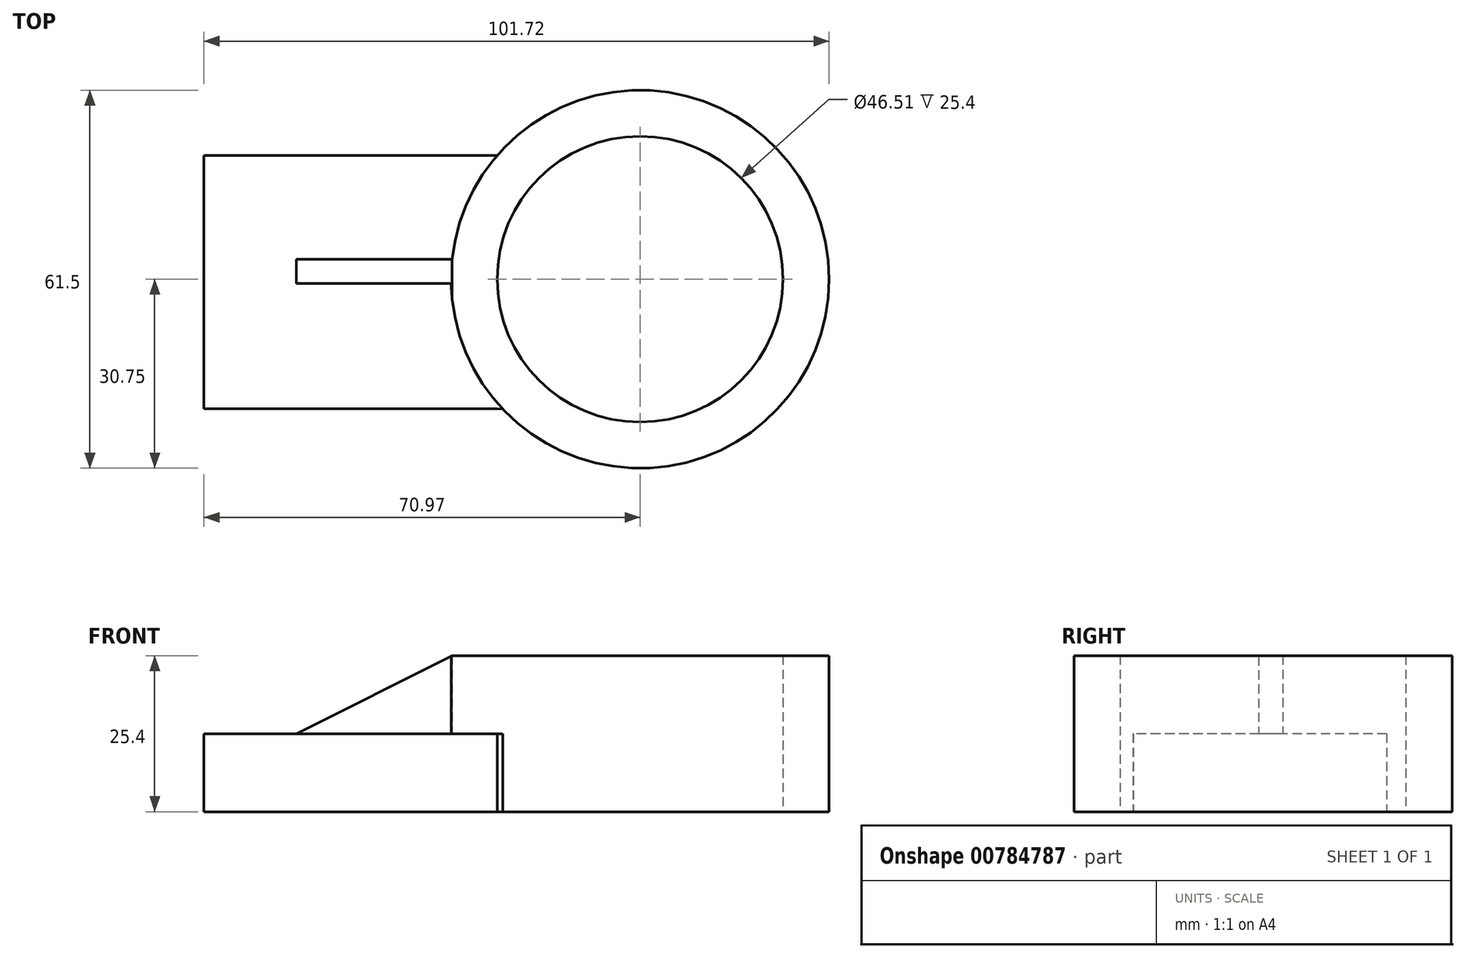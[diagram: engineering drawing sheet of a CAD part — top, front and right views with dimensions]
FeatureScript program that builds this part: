
annotation { "Feature Type Name" : "Feature", "Feature Type Description" : "" }
export const myFeature = defineFeature(function(context is Context, id is Id, definition is map)
    precondition{}
    {
        {
            var Q0;
            Q0=qCreatedBy(makeId("Top.planeOp"),FACE);
            var sketch = newSketch(context, id + "F0", { "sketchPlane" : qUnion([Q0])});
            skLineSegment(sketch, "E0.bottom", {"start": v(-70.97, 20.12) * mm, "end": v(-23.26, 20.12) * mm});
            skLineSegment(sketch, "E0.top", {"start": v(-70.97, -21.09) * mm, "end": v(-23.26, -21.09) * mm});
            skLineSegment(sketch, "E0.left", {"start": v(-70.97, 20.12) * mm, "end": v(-70.97, -21.09) * mm});
            skCircle(sketch, "E1", {"center": v(0, 0) * mm, "radius": 23.26 * mm});
            skCircle(sketch, "E2", {"center": v(0, 0) * mm, "radius": 30.75 * mm});
            skLineSegment(sketch, "E3", {"start": v(-23.26, -21.09) * mm, "end": v(-22.34, -21.13) * mm});
            skSolve(sketch);
        }
        {
            var Q0;
            Q0=makeQuery(id+"F0.imprint","IMPRINT",FACE,{"disambiguationData":[TD([[makeQuery(id+"F0.imprint","IMPRINT",EDGE,{"derivedFrom":sQuery(id+"F0.wireOp",EDGE,"E1")}),-1.0]])]});
            extrude(context, id + "F1", {"entities" : qUnion([Q0]), "depth" : 25.4 * mm, "offsetDistance" : 25.4 * mm});
        }
        {
            var Q0;
            {var subQ1=sQuery(id+"F0.wireOp",EDGE,"E0.bottom");Q0=makeQuery(id+"F0.imprint","IMPRINT",FACE,{"disambiguationData":[TD([[makeQuery(id+"F0.imprint","IMPRINT",EDGE,{"derivedFrom":subQ1}),-1.0]])]});}
            extrude(context, id + "F2", {"entities" : qUnion([Q0]), "operationType" : NewBodyOperationType.ADD, "depth" : 12.7 * mm, "offsetDistance" : 25.4 * mm});
        }
        {
            var Q0;
            Q0=makeQuery(id+"F2.opExtrude","CAP_FACE",FACE,{"disambiguationData":[OSD([sQuery(id+"F0.wireOp",EDGE,"E0.bottom"),sQuery(id+"F0.wireOp",EDGE,"E0.top"),sQuery(id+"F0.wireOp",EDGE,"E0.left"),sQuery(id+"F0.wireOp",EDGE,"E2"),sQuery(id+"F0.wireOp",EDGE,"E3")])],"isStart":false});
            var sketch = newSketch(context, id + "F3", { "sketchPlane" : qUnion([Q0])});
            skPoint(sketch, "E4.oppositeSnap0", {"position": v(-30.75, -0.68) * mm});
            skLineSegment(sketch, "E4.bottom", {"start": v(-30.58, 3.25) * mm, "end": v(-55.97, 3.25) * mm});
            skLineSegment(sketch, "E4.top", {"start": v(-30.58, -0.68) * mm, "end": v(-55.97, -0.68) * mm});
            skLineSegment(sketch, "E4.left", {"start": v(-30.58, 3.25) * mm, "end": v(-30.58, -0.68) * mm});
            skLineSegment(sketch, "E4.right", {"start": v(-55.97, 3.25) * mm, "end": v(-55.97, -0.68) * mm});
            skSolve(sketch);
        }
        {
            var Q0;
            {var subQ0=sQuery(id+"F3.wireOp",EDGE,"E4.bottom");Q0=makeQuery(id+"F3.imprint","IMPRINT",FACE,{"disambiguationData":[TD([[makeQuery(id+"F3.imprint","IMPRINT",EDGE,{"derivedFrom":subQ0}),1.0]])]});}
            extrude(context, id + "F4", {"entities" : qUnion([Q0]), "operationType" : NewBodyOperationType.ADD, "depth" : 12.7 * mm, "offsetDistance" : 25.4 * mm});
        }
        {
            var Q0;
            Q0=makeQuery(id+"F4.opExtrude","SWEPT_FACE",FACE,{"disambiguationData":[OSD([sQuery(id+"F3.wireOp",EDGE,"E4.bottom")])]});
            var sketch = newSketch(context, id + "F5", { "sketchPlane" : qUnion([Q0])});
            skLineSegment(sketch, "E5", {"start": v(30.58, 25.4) * mm, "end": v(55.97, 12.7) * mm});
            skSolve(sketch);
        }
        {
            var Q0;
            Q0=makeQuery(id+"F5.imprint","IMPRINT",FACE,{"disambiguationData":[TD([[makeQuery(id+"F5.imprint","IMPRINT",EDGE,{"derivedFrom":sQuery(id+"F5.wireOp",EDGE,"E5")}),1.0]])]});
            extrude(context, id + "F6", {"entities" : qUnion([Q0]), "operationType" : NewBodyOperationType.REMOVE, "oppositeDirection" : true, "depth" : 25.4 * mm, "offsetDistance" : 25.4 * mm});
        }
    });
